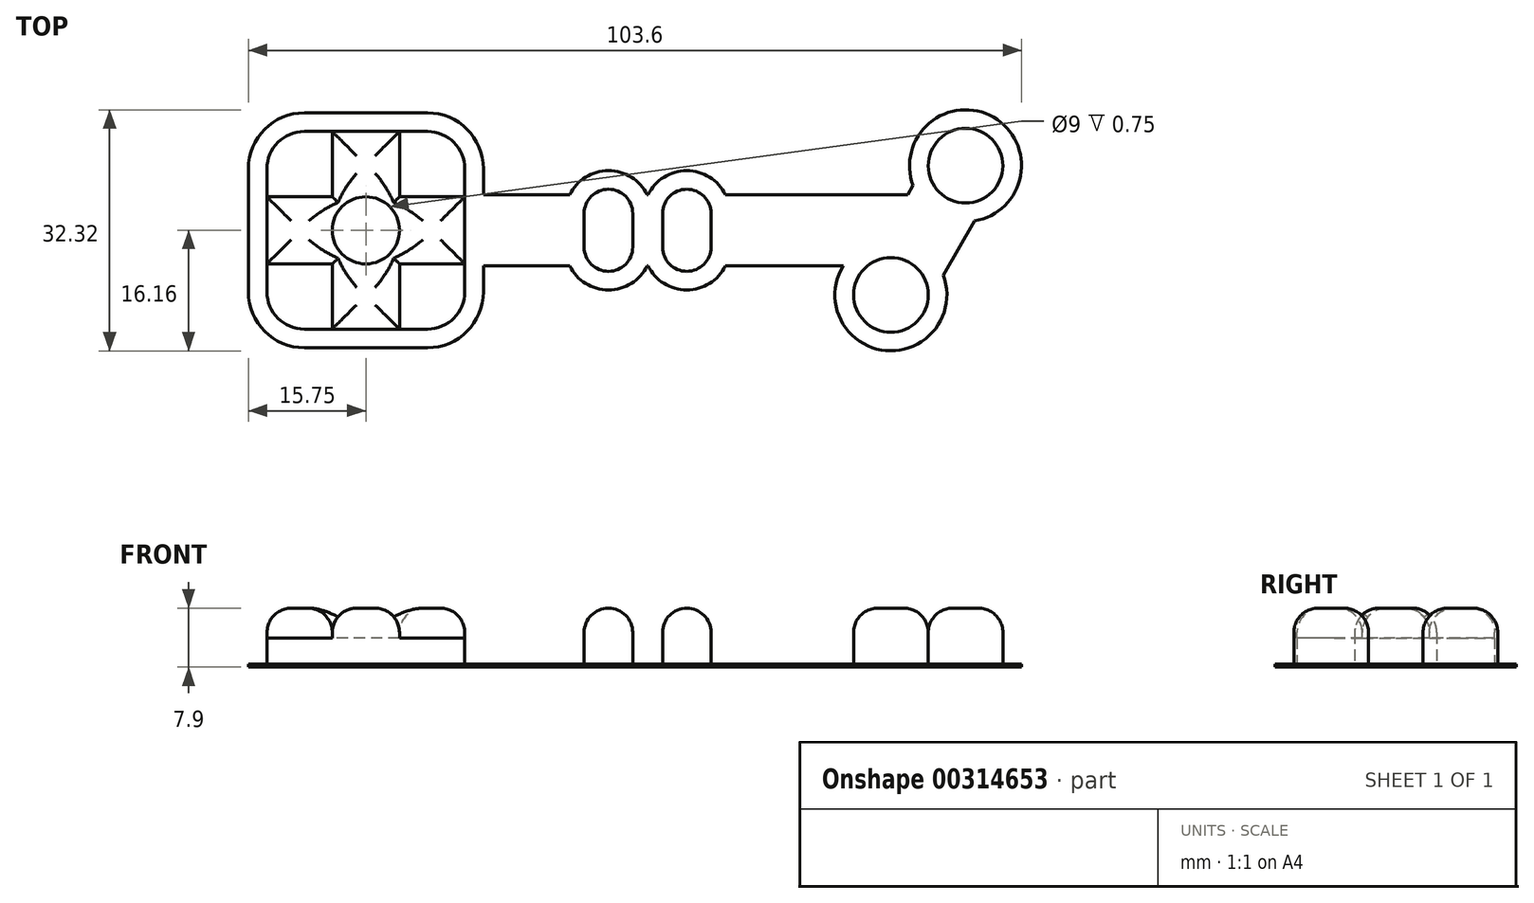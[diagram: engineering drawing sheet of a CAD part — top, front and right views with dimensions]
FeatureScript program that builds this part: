
annotation { "Feature Type Name" : "Feature", "Feature Type Description" : "" }
export const myFeature = defineFeature(function(context is Context, id is Id, definition is map)
    precondition{}
    {
        {
            var Q0;
            Q0=qCreatedBy(makeId("Top.planeOp"),FACE);
            var sketch = newSketch(context, id + "F0", { "sketchPlane" : qUnion([Q0])});
            skLineSegment(sketch, "E0.bottom", {"start": v(8.25, -13.25) * mm, "end": v(-8.25, -13.25) * mm});
            skLineSegment(sketch, "E0.top", {"start": v(8.25, 13.25) * mm, "end": v(-8.25, 13.25) * mm});
            skLineSegment(sketch, "E0.left", {"start": v(13.25, -8.25) * mm, "end": v(13.25, -2.25) * mm});
            skLineSegment(sketch, "E0.right", {"start": v(-13.25, -8.25) * mm, "end": v(-13.25, 8.25) * mm});
            skPoint(sketch, "E0.middle", {"position": v(0, 0) * mm});
            skPoint(sketch, "E1.visualSharp", {"position": v(-13.25, 13.25) * mm});
            skArc(sketch, "E1.filletArc", {"start": v(-8.25, 13.25) * mm, "mid": v(-11.79, 11.79) * mm, "end": v(-13.25, 8.25) * mm});
            skPoint(sketch, "E2.visualSharp", {"position": v(13.25, 13.25) * mm});
            skArc(sketch, "E2.filletArc", {"start": v(13.25, 8.25) * mm, "mid": v(11.79, 11.79) * mm, "end": v(8.25, 13.25) * mm});
            skPoint(sketch, "E3.visualSharp", {"position": v(13.25, -13.25) * mm});
            skArc(sketch, "E3.filletArc", {"start": v(8.25, -13.25) * mm, "mid": v(11.79, -11.79) * mm, "end": v(13.25, -8.25) * mm});
            skPoint(sketch, "E4.visualSharp", {"position": v(-13.25, -13.25) * mm});
            skArc(sketch, "E4.filletArc", {"start": v(-13.25, -8.25) * mm, "mid": v(-11.79, -11.79) * mm, "end": v(-8.25, -13.25) * mm});
            skCircle(sketch, "E5", {"center": v(0, 0) * mm, "radius": 4.5 * mm});
            skLineSegment(sketch, "E6", {"start": v(-4.5, 13.25) * mm, "end": v(-4.5, -13.25) * mm});
            skLineSegment(sketch, "E7", {"start": v(4.5, 13.25) * mm, "end": v(4.5, -13.25) * mm});
            skLineSegment(sketch, "E8", {"start": v(-13.25, 4.5) * mm, "end": v(13.25, 4.5) * mm});
            skLineSegment(sketch, "E9", {"start": v(-13.25, -4.5) * mm, "end": v(13.25, -4.5) * mm});
            skLineSegment(sketch, "E10", {"start": v(-61.71, 0) * mm, "end": v(60.36, 0) * mm, "construction": true});
            skLineSegment(sketch, "E11", {"start": v(13.25, 2.25) * mm, "end": v(29.25, 2.25) * mm});
            skLineSegment(sketch, "E12.bottom", {"start": v(29.25, 2.25) * mm, "end": v(35.75, 2.25) * mm});
            skLineSegment(sketch, "E12.top", {"start": v(29.25, -2.25) * mm, "end": v(35.75, -2.25) * mm});
            skLineSegment(sketch, "E12.left", {"start": v(29.25, 2.25) * mm, "end": v(29.25, -2.25) * mm});
            skLineSegment(sketch, "E12.right", {"start": v(35.75, 2.25) * mm, "end": v(35.75, -2.25) * mm});
            skLineSegment(sketch, "E13", {"start": v(37.75, 8.35) * mm, "end": v(37.75, -9.7) * mm, "construction": true});
            skLineSegment(sketch, "E14.MirrorCS", {"start": v(39.75, 2.25) * mm, "end": v(39.75, -2.25) * mm});
            skLineSegment(sketch, "E15.MirrorCS", {"start": v(46.25, -2.25) * mm, "end": v(39.75, -2.25) * mm});
            skLineSegment(sketch, "E16.MirrorCS", {"start": v(46.25, 2.25) * mm, "end": v(39.75, 2.25) * mm});
            skLineSegment(sketch, "E17.MirrorCS", {"start": v(46.25, 2.25) * mm, "end": v(46.25, -45.9) * mm});
            skLineSegment(sketch, "E18.MirrorCS", {"start": v(13.25, -2.25) * mm, "end": v(29.25, -2.25) * mm});
            skLineSegment(sketch, "E19", {"start": v(35.75, 2.25) * mm, "end": v(39.75, 2.25) * mm});
            skLineSegment(sketch, "E20", {"start": v(39.75, -2.25) * mm, "end": v(35.75, -2.25) * mm});
            skArc(sketch, "E21", {"start": v(35.75, 2.25) * mm, "mid": v(32.5, 5.5) * mm, "end": v(29.25, 2.25) * mm});
            skArc(sketch, "E22.MirrorCS", {"start": v(39.75, 2.25) * mm, "mid": v(43, 5.5) * mm, "end": v(46.25, 2.25) * mm});
            skLineSegment(sketch, "E23.MirrorCS", {"start": v(137.21, 0) * mm, "end": v(15.14, 0) * mm, "construction": true});
            skArc(sketch, "E24.MirrorCS", {"start": v(35.75, -2.25) * mm, "mid": v(32.5, -5.5) * mm, "end": v(29.25, -2.25) * mm});
            skArc(sketch, "E25.MirrorCS", {"start": v(39.75, -2.25) * mm, "mid": v(43, -5.5) * mm, "end": v(46.25, -2.25) * mm});
            skLineSegment(sketch, "E26", {"start": v(46.25, 2.25) * mm, "end": v(74.05, 2.25) * mm});
            skLineSegment(sketch, "E27", {"start": v(80.35, 8.66) * mm, "end": v(70.35, -8.66) * mm, "construction": true});
            skPoint(sketch, "E28", {"position": v(75.35, 0) * mm});
            skLineSegment(sketch, "E29", {"start": v(76.17, 5.92) * mm, "end": v(74.05, 2.25) * mm});
            skLineSegment(sketch, "E30.MirrorCS", {"start": v(80.06, 3.67) * mm, "end": v(74.53, -5.92) * mm});
            skPoint(sketch, "E31", {"position": v(72.75, 0) * mm});
            skPoint(sketch, "E32.orphan", {"position": v(46.25, -2.25) * mm});
            skLineSegment(sketch, "E33", {"start": v(46.25, -2.25) * mm, "end": v(71.45, -2.25) * mm});
            skLineSegment(sketch, "E34", {"start": v(71.45, -2.25) * mm, "end": v(70.63, -3.67) * mm});
            skLineSegment(sketch, "E35", {"start": v(74.05, 2.25) * mm, "end": v(71.45, -2.25) * mm});
            skArc(sketch, "E36", {"start": v(76.17, 5.92) * mm, "mid": v(77.85, 4.33) * mm, "end": v(80.06, 3.67) * mm});
            skArc(sketch, "E37", {"start": v(80.06, 3.67) * mm, "mid": v(82.85, 13) * mm, "end": v(76.17, 5.92) * mm});
            skLineSegment(sketch, "E38", {"start": v(70.63, -3.67) * mm, "end": v(70.63, -3.67) * mm});
            skArc(sketch, "E39", {"start": v(70.63, -3.67) * mm, "mid": v(67.85, -13) * mm, "end": v(74.53, -5.92) * mm});
            skArc(sketch, "E40", {"start": v(74.53, -5.92) * mm, "mid": v(72.85, -4.33) * mm, "end": v(70.63, -3.67) * mm});
            skLineSegment(sketch, "E41", {"start": v(13.25, 2.25) * mm, "end": v(13.25, 8.25) * mm});
            skLineSegment(sketch, "E42", {"start": v(13.25, -2.25) * mm, "end": v(13.25, 2.25) * mm});
            skLineSegment(sketch, "E43.0", {"start": v(37.82, -4.75) * mm, "end": v(37.68, -4.75) * mm});
            skArc(sketch, "E43.1", {"start": v(37.68, -4.75) * mm, "mid": v(32.5, -8) * mm, "end": v(27.32, -4.75) * mm});
            skLineSegment(sketch, "E43.2", {"start": v(15.75, -4.75) * mm, "end": v(27.32, -4.75) * mm});
            skLineSegment(sketch, "E43.3", {"start": v(15.75, -8.25) * mm, "end": v(15.75, -4.75) * mm});
            skArc(sketch, "E43.4", {"start": v(8.25, -15.75) * mm, "mid": v(13.55, -13.55) * mm, "end": v(15.75, -8.25) * mm});
            skLineSegment(sketch, "E43.5", {"start": v(8.25, -15.75) * mm, "end": v(-8.25, -15.75) * mm});
            skLineSegment(sketch, "E43.6", {"start": v(8.25, 15.75) * mm, "end": v(-8.25, 15.75) * mm});
            skArc(sketch, "E43.7", {"start": v(-8.25, 15.75) * mm, "mid": v(-13.55, 13.55) * mm, "end": v(-15.75, 8.25) * mm});
            skLineSegment(sketch, "E43.8", {"start": v(-15.75, -8.25) * mm, "end": v(-15.75, 8.25) * mm});
            skArc(sketch, "E43.9", {"start": v(-15.75, -8.25) * mm, "mid": v(-13.55, -13.55) * mm, "end": v(-8.25, -15.75) * mm});
            skArc(sketch, "E43.10", {"start": v(15.75, 8.25) * mm, "mid": v(13.55, 13.55) * mm, "end": v(8.25, 15.75) * mm});
            skArc(sketch, "E43.11", {"start": v(37.82, -4.75) * mm, "mid": v(43, -8) * mm, "end": v(48.18, -4.75) * mm});
            skLineSegment(sketch, "E43.12", {"start": v(48.18, -4.75) * mm, "end": v(63.95, -4.75) * mm});
            skArc(sketch, "E43.13", {"start": v(63.95, -4.75) * mm, "mid": v(69.65, -16.13) * mm, "end": v(77.36, -6) * mm});
            skLineSegment(sketch, "E43.14", {"start": v(81.56, 1.26) * mm, "end": v(77.36, -6) * mm});
            skArc(sketch, "E43.15", {"start": v(81.56, 1.26) * mm, "mid": v(84.1, 15.16) * mm, "end": v(73.33, 6) * mm});
            skLineSegment(sketch, "E43.16", {"start": v(73.33, 6) * mm, "end": v(72.6, 4.75) * mm});
            skLineSegment(sketch, "E43.17", {"start": v(48.18, 4.75) * mm, "end": v(72.6, 4.75) * mm});
            skArc(sketch, "E43.18", {"start": v(37.82, 4.75) * mm, "mid": v(43, 8) * mm, "end": v(48.18, 4.75) * mm});
            skLineSegment(sketch, "E43.19", {"start": v(37.68, 4.75) * mm, "end": v(37.82, 4.75) * mm});
            skArc(sketch, "E43.20", {"start": v(37.68, 4.75) * mm, "mid": v(32.5, 8) * mm, "end": v(27.32, 4.75) * mm});
            skLineSegment(sketch, "E43.21", {"start": v(15.75, 4.75) * mm, "end": v(27.32, 4.75) * mm});
            skLineSegment(sketch, "E43.22", {"start": v(15.75, 4.75) * mm, "end": v(15.75, 8.25) * mm});
            skSolve(sketch);
        }
        {
            var Q0;
            Q0=makeQuery(id+"F0.imprint","IMPRINT",FACE,{"disambiguationData":[TD([[makeQuery(id+"F0.imprint","IMPRINT",EDGE,{"derivedFrom":sQuery(id+"F0.wireOp",EDGE,"E36")}),1.0]])]});
            var Q1;
            {var subQ0=sQuery(id+"F0.wireOp",EDGE,"E8");var subQ1=sQuery(id+"F0.wireOp",EDGE,"E5");var subQ2=makeQuery(id+"F0.imprint","INTERSECT",VERTEX,{"derivedFrom":[subQ1,subQ0]});Q1=makeQuery(id+"F0.imprint","IMPRINT",FACE,{"disambiguationData":[TD([[makeQuery(id+"F0.imprint","IMPRINT",EDGE,{"disambiguationData":[TD([[subQ2,1.0]])],"derivedFrom":subQ1}),-1.0]])]});}
            var Q2;
            Q2=makeQuery(id+"F0.imprint","IMPRINT",FACE,{"disambiguationData":[TD([[makeQuery(id+"F0.imprint","IMPRINT",EDGE,{"derivedFrom":sQuery(id+"F0.wireOp",EDGE,"E11")}),-1.0]])]});
            var Q3;
            Q3=makeQuery(id+"F0.imprint","IMPRINT",FACE,{"disambiguationData":[TD([[makeQuery(id+"F0.imprint","IMPRINT",EDGE,{"derivedFrom":sQuery(id+"F0.wireOp",EDGE,"E39")}),1.0]])]});
            var Q4;
            {var subQ0=sQuery(id+"F0.wireOp",EDGE,"E4.filletArc");Q4=makeQuery(id+"F0.imprint","IMPRINT",FACE,{"disambiguationData":[TD([[makeQuery(id+"F0.imprint","IMPRINT",EDGE,{"derivedFrom":subQ0}),1.0]])]});}
            var Q5;
            Q5=makeQuery(id+"F0.imprint","IMPRINT",FACE,{"disambiguationData":[TD([[makeQuery(id+"F0.imprint","IMPRINT",EDGE,{"derivedFrom":sQuery(id+"F0.wireOp",EDGE,"E12.top")}),-1.0]])]});
            var Q6;
            {var subQ2=sQuery(id+"F0.wireOp",EDGE,"E26");Q6=makeQuery(id+"F0.imprint","IMPRINT",FACE,{"disambiguationData":[TD([[makeQuery(id+"F0.imprint","IMPRINT",EDGE,{"derivedFrom":subQ2}),-1.0]])]});}
            var Q7;
            {var subQ5=sQuery(id+"F0.wireOp",EDGE,"E2.filletArc");Q7=makeQuery(id+"F0.imprint","IMPRINT",FACE,{"disambiguationData":[TD([[makeQuery(id+"F0.imprint","IMPRINT",EDGE,{"derivedFrom":subQ5}),1.0]])]});}
            var Q8;
            {var subQ0=sQuery(id+"F0.wireOp",EDGE,"E7");var subQ1=sQuery(id+"F0.wireOp",EDGE,"E5");var subQ2=makeQuery(id+"F0.imprint","INTERSECT",VERTEX,{"derivedFrom":[subQ1,subQ0]});Q8=makeQuery(id+"F0.imprint","IMPRINT",FACE,{"disambiguationData":[TD([[makeQuery(id+"F0.imprint","IMPRINT",EDGE,{"disambiguationData":[TD([[subQ2,1.0]])],"derivedFrom":subQ1}),-1.0]])]});}
            var Q9;
            {var subQ0=sQuery(id+"F0.wireOp",EDGE,"E8");var subQ1=sQuery(id+"F0.wireOp",EDGE,"E5");var subQ2=makeQuery(id+"F0.imprint","INTERSECT",VERTEX,{"derivedFrom":[subQ1,subQ0]});Q9=makeQuery(id+"F0.imprint","IMPRINT",FACE,{"disambiguationData":[TD([[makeQuery(id+"F0.imprint","IMPRINT",EDGE,{"disambiguationData":[TD([[subQ2,-1.0]])],"derivedFrom":subQ1}),-1.0]])]});}
            var Q10;
            Q10=makeQuery(id+"F0.imprint","IMPRINT",FACE,{"disambiguationData":[TD([[makeQuery(id+"F0.imprint","IMPRINT",EDGE,{"derivedFrom":sQuery(id+"F0.wireOp",EDGE,"E15.MirrorCS")}),1.0]])]});
            var Q11;
            Q11=makeQuery(id+"F0.imprint","IMPRINT",FACE,{"disambiguationData":[TD([[makeQuery(id+"F0.imprint","IMPRINT",EDGE,{"derivedFrom":sQuery(id+"F0.wireOp",EDGE,"E16.MirrorCS")}),-1.0]])]});
            var Q12;
            {var subQ0=sQuery(id+"F0.wireOp",EDGE,"E6");var subQ1=sQuery(id+"F0.wireOp",EDGE,"E5");var subQ2=makeQuery(id+"F0.imprint","INTERSECT",VERTEX,{"derivedFrom":[subQ1,subQ0]});Q12=makeQuery(id+"F0.imprint","IMPRINT",FACE,{"disambiguationData":[TD([[makeQuery(id+"F0.imprint","IMPRINT",EDGE,{"disambiguationData":[TD([[subQ2,-1.0]])],"derivedFrom":subQ1}),-1.0]])]});}
            var Q13;
            {var subQ17=sQuery(id+"F0.wireOp",EDGE,"E1.filletArc");Q13=makeQuery(id+"F0.imprint","IMPRINT",FACE,{"disambiguationData":[TD([[makeQuery(id+"F0.imprint","IMPRINT",EDGE,{"derivedFrom":subQ17}),-1.0]])]});}
            var Q14;
            {var subQ0=sQuery(id+"F0.wireOp",EDGE,"E3.filletArc");Q14=makeQuery(id+"F0.imprint","IMPRINT",FACE,{"disambiguationData":[TD([[makeQuery(id+"F0.imprint","IMPRINT",EDGE,{"derivedFrom":subQ0}),1.0]])]});}
            var Q15;
            Q15=makeQuery(id+"F0.imprint","IMPRINT",FACE,{"disambiguationData":[TD([[makeQuery(id+"F0.imprint","IMPRINT",EDGE,{"derivedFrom":sQuery(id+"F0.wireOp",EDGE,"E12.right")}),1.0]])]});
            var Q16;
            Q16=makeQuery(id+"F0.imprint","IMPRINT",FACE,{"disambiguationData":[TD([[makeQuery(id+"F0.imprint","IMPRINT",EDGE,{"derivedFrom":sQuery(id+"F0.wireOp",EDGE,"E12.bottom")}),1.0]])]});
            var Q17;
            Q17=makeQuery(id+"F0.imprint","IMPRINT",FACE,{"disambiguationData":[TD([[makeQuery(id+"F0.imprint","IMPRINT",EDGE,{"derivedFrom":sQuery(id+"F0.wireOp",EDGE,"E12.bottom")}),-1.0]])]});
            var Q18;
            {var subQ5=sQuery(id+"F0.wireOp",EDGE,"E1.filletArc");Q18=makeQuery(id+"F0.imprint","IMPRINT",FACE,{"disambiguationData":[TD([[makeQuery(id+"F0.imprint","IMPRINT",EDGE,{"derivedFrom":subQ5}),1.0]])]});}
            var Q19;
            Q19=makeQuery(id+"F0.imprint","IMPRINT",FACE,{"disambiguationData":[TD([[makeQuery(id+"F0.imprint","IMPRINT",EDGE,{"derivedFrom":sQuery(id+"F0.wireOp",EDGE,"E14.MirrorCS")}),1.0]])]});
            var Q20;
            {var subQ2=sQuery(id+"F0.wireOp",EDGE,"E6");var subQ4=sQuery(id+"F0.wireOp",EDGE,"E0.bottom");var subQ5=makeQuery(id+"F0.imprint","INTERSECT",VERTEX,{"derivedFrom":[subQ4,subQ2]});Q20=makeQuery(id+"F0.imprint","IMPRINT",FACE,{"disambiguationData":[TD([[makeQuery(id+"F0.imprint","IMPRINT",EDGE,{"disambiguationData":[TD([[subQ5,1.0]])],"derivedFrom":subQ4}),-1.0]])]});}
            var Q21;
            Q21=makeQuery(id+"F0.imprint","IMPRINT",FACE,{"disambiguationData":[TD([[makeQuery(id+"F0.imprint","IMPRINT",EDGE,{"derivedFrom":sQuery(id+"F0.wireOp",EDGE,"E29")}),1.0]])]});
            var Q22;
            {var subQ5=sQuery(id+"F0.wireOp",EDGE,"E42");Q22=makeQuery(id+"F0.imprint","IMPRINT",FACE,{"disambiguationData":[TD([[makeQuery(id+"F0.imprint","IMPRINT",EDGE,{"derivedFrom":subQ5}),1.0]])]});}
            var Q23;
            {var subQ0=sQuery(id+"F0.wireOp",EDGE,"E5");var subQ1=makeQuery(id+"F0.imprint","INTERSECT",VERTEX,{"derivedFrom":[subQ0,sQuery(id+"F0.wireOp",EDGE,"E8")]});Q23=makeQuery(id+"F0.imprint","IMPRINT",FACE,{"disambiguationData":[TD([[makeQuery(id+"F0.imprint","IMPRINT",EDGE,{"disambiguationData":[TD([[subQ1,1.0]])],"derivedFrom":subQ0}),1.0]])]});}
            var Q24;
            {var subQ2=sQuery(id+"F0.wireOp",EDGE,"E6");var subQ5=sQuery(id+"F0.wireOp",EDGE,"E0.top");var subQ8=makeQuery(id+"F0.imprint","INTERSECT",VERTEX,{"derivedFrom":[subQ5,subQ2]});Q24=makeQuery(id+"F0.imprint","IMPRINT",FACE,{"disambiguationData":[TD([[makeQuery(id+"F0.imprint","IMPRINT",EDGE,{"disambiguationData":[TD([[subQ8,1.0]])],"derivedFrom":subQ5}),1.0]])]});}
            var Q25;
            {var subQ0=sQuery(id+"F0.wireOp",EDGE,"E8");var subQ1=sQuery(id+"F0.wireOp",EDGE,"E0.right");var subQ2=makeQuery(id+"F0.imprint","INTERSECT",VERTEX,{"derivedFrom":[subQ1,subQ0]});Q25=makeQuery(id+"F0.imprint","IMPRINT",FACE,{"disambiguationData":[TD([[makeQuery(id+"F0.imprint","IMPRINT",EDGE,{"disambiguationData":[TD([[subQ2,1.0]])],"derivedFrom":subQ1}),-1.0]])]});}
            extrude(context, id + "F1", {"entities" : qUnion([Q0, Q1, Q2, Q3, Q4, Q5, Q6, Q7, Q8, Q9, Q10, Q11, Q12, Q13, Q14, Q15, Q16, Q17, Q18, Q19, Q20, Q21, Q22, Q23, Q24, Q25]), "depth" : 0.4 * mm});
        }
        {
            var Q0;
            Q0=makeQuery(id+"F1.opExtrude","CAP_FACE",FACE,{"disambiguationData":[OSD([sQuery(id+"F0.wireOp",EDGE,"E43.0"),sQuery(id+"F0.wireOp",EDGE,"E43.1"),sQuery(id+"F0.wireOp",EDGE,"E43.2"),sQuery(id+"F0.wireOp",EDGE,"E43.3"),sQuery(id+"F0.wireOp",EDGE,"E43.4"),sQuery(id+"F0.wireOp",EDGE,"E43.5"),sQuery(id+"F0.wireOp",EDGE,"E43.6"),sQuery(id+"F0.wireOp",EDGE,"E43.7"),sQuery(id+"F0.wireOp",EDGE,"E43.8"),sQuery(id+"F0.wireOp",EDGE,"E43.9"),sQuery(id+"F0.wireOp",EDGE,"E43.10"),sQuery(id+"F0.wireOp",EDGE,"E43.11"),sQuery(id+"F0.wireOp",EDGE,"E43.12"),sQuery(id+"F0.wireOp",EDGE,"E43.13"),sQuery(id+"F0.wireOp",EDGE,"E43.14"),sQuery(id+"F0.wireOp",EDGE,"E43.15"),sQuery(id+"F0.wireOp",EDGE,"E43.16"),sQuery(id+"F0.wireOp",EDGE,"E43.17"),sQuery(id+"F0.wireOp",EDGE,"E43.18"),sQuery(id+"F0.wireOp",EDGE,"E43.19"),sQuery(id+"F0.wireOp",EDGE,"E43.20"),sQuery(id+"F0.wireOp",EDGE,"E43.21"),sQuery(id+"F0.wireOp",EDGE,"E43.22")])],"isStart":false});
            var sketch = newSketch(context, id + "F2", { "sketchPlane" : qUnion([Q0])});
            skLineSegment(sketch, "E44.0", {"start": v(8.25, -13.25) * mm, "end": v(-8.25, -13.25) * mm});
            skLineSegment(sketch, "E44.1", {"start": v(8.25, 13.25) * mm, "end": v(-8.25, 13.25) * mm});
            skLineSegment(sketch, "E44.2", {"start": v(13.25, -8.25) * mm, "end": v(13.25, -2.25) * mm});
            skLineSegment(sketch, "E44.3", {"start": v(-13.25, -8.25) * mm, "end": v(-13.25, 8.25) * mm});
            skPoint(sketch, "E44.4", {"position": v(0, 0) * mm});
            skPoint(sketch, "E44.5", {"position": v(-13.25, 13.25) * mm});
            skArc(sketch, "E44.6", {"start": v(-8.25, 13.25) * mm, "mid": v(-11.79, 11.79) * mm, "end": v(-13.25, 8.25) * mm});
            skPoint(sketch, "E44.7", {"position": v(13.25, 13.25) * mm});
            skArc(sketch, "E44.8", {"start": v(13.25, 8.25) * mm, "mid": v(11.79, 11.79) * mm, "end": v(8.25, 13.25) * mm});
            skPoint(sketch, "E44.9", {"position": v(13.25, -13.25) * mm});
            skArc(sketch, "E44.10", {"start": v(8.25, -13.25) * mm, "mid": v(11.79, -11.79) * mm, "end": v(13.25, -8.25) * mm});
            skPoint(sketch, "E44.11", {"position": v(-13.25, -13.25) * mm});
            skArc(sketch, "E44.12", {"start": v(-13.25, -8.25) * mm, "mid": v(-11.79, -11.79) * mm, "end": v(-8.25, -13.25) * mm});
            skCircle(sketch, "E44.13", {"center": v(0, 0) * mm, "radius": 4.5 * mm});
            skLineSegment(sketch, "E44.14", {"start": v(-4.5, 13.25) * mm, "end": v(-4.5, -13.25) * mm});
            skLineSegment(sketch, "E44.15", {"start": v(4.5, 13.25) * mm, "end": v(4.5, -13.25) * mm});
            skLineSegment(sketch, "E44.16", {"start": v(-13.25, 4.5) * mm, "end": v(13.25, 4.5) * mm});
            skLineSegment(sketch, "E44.17", {"start": v(-13.25, -4.5) * mm, "end": v(13.25, -4.5) * mm});
            skLineSegment(sketch, "E44.19", {"start": v(13.25, 2.25) * mm, "end": v(29.25, 2.25) * mm});
            skLineSegment(sketch, "E44.20", {"start": v(29.25, 2.25) * mm, "end": v(35.75, 2.25) * mm});
            skLineSegment(sketch, "E44.21", {"start": v(29.25, -2.25) * mm, "end": v(35.75, -2.25) * mm});
            skLineSegment(sketch, "E44.22", {"start": v(29.25, 2.25) * mm, "end": v(29.25, -2.25) * mm});
            skLineSegment(sketch, "E44.23", {"start": v(35.75, 2.25) * mm, "end": v(35.75, -2.25) * mm});
            skLineSegment(sketch, "E44.25", {"start": v(39.75, 2.25) * mm, "end": v(39.75, -2.25) * mm});
            skLineSegment(sketch, "E44.26", {"start": v(46.25, -2.25) * mm, "end": v(39.75, -2.25) * mm});
            skLineSegment(sketch, "E44.27", {"start": v(46.25, 2.25) * mm, "end": v(39.75, 2.25) * mm});
            skLineSegment(sketch, "E44.28", {"start": v(46.25, 2.25) * mm, "end": v(46.25, -2.25) * mm});
            skLineSegment(sketch, "E44.29", {"start": v(13.25, -2.25) * mm, "end": v(29.25, -2.25) * mm});
            skLineSegment(sketch, "E44.30", {"start": v(35.75, 2.25) * mm, "end": v(39.75, 2.25) * mm});
            skLineSegment(sketch, "E44.31", {"start": v(39.75, -2.25) * mm, "end": v(35.75, -2.25) * mm});
            skArc(sketch, "E44.32", {"start": v(35.75, 2.25) * mm, "mid": v(32.5, 5.5) * mm, "end": v(29.25, 2.25) * mm});
            skArc(sketch, "E44.33", {"start": v(39.75, 2.25) * mm, "mid": v(43, 5.5) * mm, "end": v(46.25, 2.25) * mm});
            skLineSegment(sketch, "E44.34", {"start": v(80.83, 0) * mm, "end": v(15.14, 0) * mm});
            skArc(sketch, "E44.35", {"start": v(35.75, -2.25) * mm, "mid": v(32.5, -5.5) * mm, "end": v(29.25, -2.25) * mm});
            skArc(sketch, "E44.36", {"start": v(39.75, -2.25) * mm, "mid": v(43, -5.5) * mm, "end": v(46.25, -2.25) * mm});
            skLineSegment(sketch, "E44.37", {"start": v(46.25, 2.25) * mm, "end": v(74.05, 2.25) * mm});
            skLineSegment(sketch, "E44.38", {"start": v(80.35, 8.66) * mm, "end": v(70.35, -8.66) * mm});
            skPoint(sketch, "E44.39", {"position": v(75.35, 0) * mm});
            skLineSegment(sketch, "E44.40", {"start": v(76.17, 5.92) * mm, "end": v(74.05, 2.25) * mm});
            skLineSegment(sketch, "E44.41", {"start": v(80.06, 3.67) * mm, "end": v(74.53, -5.92) * mm});
            skPoint(sketch, "E44.42", {"position": v(72.75, 0) * mm});
            skPoint(sketch, "E44.43", {"position": v(46.25, -2.25) * mm});
            skLineSegment(sketch, "E44.44", {"start": v(46.25, -2.25) * mm, "end": v(71.45, -2.25) * mm});
            skLineSegment(sketch, "E44.45", {"start": v(71.45, -2.25) * mm, "end": v(70.63, -3.67) * mm});
            skLineSegment(sketch, "E44.46", {"start": v(74.05, 2.25) * mm, "end": v(71.45, -2.25) * mm});
            skArc(sketch, "E44.47", {"start": v(76.17, 5.92) * mm, "mid": v(77.85, 4.33) * mm, "end": v(80.06, 3.67) * mm});
            skArc(sketch, "E44.48", {"start": v(80.06, 3.67) * mm, "mid": v(82.85, 13) * mm, "end": v(76.17, 5.92) * mm});
            skPoint(sketch, "E44.49", {"position": v(70.63, -3.67) * mm});
            skArc(sketch, "E44.50", {"start": v(70.63, -3.67) * mm, "mid": v(67.85, -13) * mm, "end": v(74.53, -5.92) * mm});
            skArc(sketch, "E44.51", {"start": v(74.53, -5.92) * mm, "mid": v(72.85, -4.33) * mm, "end": v(70.63, -3.67) * mm});
            skLineSegment(sketch, "E44.52", {"start": v(13.25, 2.25) * mm, "end": v(13.25, 8.25) * mm});
            skLineSegment(sketch, "E44.53", {"start": v(13.25, -2.25) * mm, "end": v(13.25, 2.25) * mm});
            skLineSegment(sketch, "E44.54", {"start": v(37.82, -4.75) * mm, "end": v(37.68, -4.75) * mm});
            skArc(sketch, "E44.55", {"start": v(37.68, -4.75) * mm, "mid": v(32.5, -8) * mm, "end": v(27.32, -4.75) * mm});
            skLineSegment(sketch, "E44.56", {"start": v(15.75, -4.75) * mm, "end": v(27.32, -4.75) * mm});
            skLineSegment(sketch, "E44.57", {"start": v(15.75, -8.25) * mm, "end": v(15.75, -4.75) * mm});
            skArc(sketch, "E44.58", {"start": v(8.25, -15.75) * mm, "mid": v(13.55, -13.55) * mm, "end": v(15.75, -8.25) * mm});
            skLineSegment(sketch, "E44.59", {"start": v(8.25, -15.75) * mm, "end": v(-8.25, -15.75) * mm});
            skLineSegment(sketch, "E44.60", {"start": v(8.25, 15.75) * mm, "end": v(-8.25, 15.75) * mm});
            skArc(sketch, "E44.61", {"start": v(-8.25, 15.75) * mm, "mid": v(-13.55, 13.55) * mm, "end": v(-15.75, 8.25) * mm});
            skLineSegment(sketch, "E44.62", {"start": v(-15.75, -8.25) * mm, "end": v(-15.75, 8.25) * mm});
            skArc(sketch, "E44.63", {"start": v(-15.75, -8.25) * mm, "mid": v(-13.55, -13.55) * mm, "end": v(-8.25, -15.75) * mm});
            skArc(sketch, "E44.64", {"start": v(15.75, 8.25) * mm, "mid": v(13.55, 13.55) * mm, "end": v(8.25, 15.75) * mm});
            skArc(sketch, "E44.65", {"start": v(37.82, -4.75) * mm, "mid": v(43, -8) * mm, "end": v(48.18, -4.75) * mm});
            skLineSegment(sketch, "E44.66", {"start": v(48.18, -4.75) * mm, "end": v(63.95, -4.75) * mm});
            skArc(sketch, "E44.67", {"start": v(63.95, -4.75) * mm, "mid": v(69.65, -16.13) * mm, "end": v(77.36, -6) * mm});
            skLineSegment(sketch, "E44.68", {"start": v(81.56, 1.26) * mm, "end": v(77.36, -6) * mm});
            skArc(sketch, "E44.69", {"start": v(81.56, 1.26) * mm, "mid": v(84.1, 15.16) * mm, "end": v(73.33, 6) * mm});
            skLineSegment(sketch, "E44.70", {"start": v(73.33, 6) * mm, "end": v(72.6, 4.75) * mm});
            skLineSegment(sketch, "E44.71", {"start": v(48.18, 4.75) * mm, "end": v(72.6, 4.75) * mm});
            skArc(sketch, "E44.72", {"start": v(37.82, 4.75) * mm, "mid": v(43, 8) * mm, "end": v(48.18, 4.75) * mm});
            skLineSegment(sketch, "E44.73", {"start": v(37.68, 4.75) * mm, "end": v(37.82, 4.75) * mm});
            skArc(sketch, "E44.74", {"start": v(37.68, 4.75) * mm, "mid": v(32.5, 8) * mm, "end": v(27.32, 4.75) * mm});
            skLineSegment(sketch, "E44.75", {"start": v(15.75, 4.75) * mm, "end": v(27.32, 4.75) * mm});
            skLineSegment(sketch, "E44.76", {"start": v(15.75, 4.75) * mm, "end": v(15.75, 8.25) * mm});
            skSolve(sketch);
        }
        {
            var Q0;
            {var subQ5=sQuery(id+"F2.wireOp",EDGE,"E44.6");Q0=makeQuery(id+"F2.imprint","IMPRINT",FACE,{"disambiguationData":[TD([[makeQuery(id+"F2.imprint","IMPRINT",EDGE,{"derivedFrom":subQ5}),1.0]])]});}
            var Q1;
            {var subQ2=sQuery(id+"F2.wireOp",EDGE,"E44.14");var subQ5=sQuery(id+"F2.wireOp",EDGE,"E44.1");var subQ8=makeQuery(id+"F2.imprint","INTERSECT",VERTEX,{"derivedFrom":[subQ5,subQ2]});Q1=makeQuery(id+"F2.imprint","IMPRINT",FACE,{"disambiguationData":[TD([[makeQuery(id+"F2.imprint","IMPRINT",EDGE,{"disambiguationData":[TD([[subQ8,1.0]])],"derivedFrom":subQ5}),1.0]])]});}
            var Q2;
            {var subQ5=sQuery(id+"F2.wireOp",EDGE,"E44.8");Q2=makeQuery(id+"F2.imprint","IMPRINT",FACE,{"disambiguationData":[TD([[makeQuery(id+"F2.imprint","IMPRINT",EDGE,{"derivedFrom":subQ5}),1.0]])]});}
            var Q3;
            {var subQ8=sQuery(id+"F2.wireOp",EDGE,"E44.53");Q3=makeQuery(id+"F2.imprint","IMPRINT",FACE,{"disambiguationData":[TD([[makeQuery(id+"F2.imprint","IMPRINT",EDGE,{"derivedFrom":subQ8}),1.0]])]});}
            var Q4;
            {var subQ0=sQuery(id+"F2.wireOp",EDGE,"E44.10");Q4=makeQuery(id+"F2.imprint","IMPRINT",FACE,{"disambiguationData":[TD([[makeQuery(id+"F2.imprint","IMPRINT",EDGE,{"derivedFrom":subQ0}),1.0]])]});}
            var Q5;
            {var subQ2=sQuery(id+"F2.wireOp",EDGE,"E44.14");var subQ4=sQuery(id+"F2.wireOp",EDGE,"E44.0");var subQ5=makeQuery(id+"F2.imprint","INTERSECT",VERTEX,{"derivedFrom":[subQ4,subQ2]});Q5=makeQuery(id+"F2.imprint","IMPRINT",FACE,{"disambiguationData":[TD([[makeQuery(id+"F2.imprint","IMPRINT",EDGE,{"disambiguationData":[TD([[subQ5,1.0]])],"derivedFrom":subQ4}),-1.0]])]});}
            var Q6;
            {var subQ0=sQuery(id+"F2.wireOp",EDGE,"E44.12");Q6=makeQuery(id+"F2.imprint","IMPRINT",FACE,{"disambiguationData":[TD([[makeQuery(id+"F2.imprint","IMPRINT",EDGE,{"derivedFrom":subQ0}),1.0]])]});}
            var Q7;
            {var subQ0=sQuery(id+"F2.wireOp",EDGE,"E44.14");var subQ1=sQuery(id+"F2.wireOp",EDGE,"E44.13");var subQ2=makeQuery(id+"F2.imprint","INTERSECT",VERTEX,{"derivedFrom":[subQ1,subQ0]});Q7=makeQuery(id+"F2.imprint","IMPRINT",FACE,{"disambiguationData":[TD([[makeQuery(id+"F2.imprint","IMPRINT",EDGE,{"disambiguationData":[TD([[subQ2,-1.0]])],"derivedFrom":subQ1}),-1.0]])]});}
            var Q8;
            {var subQ0=sQuery(id+"F2.wireOp",EDGE,"E44.15");var subQ1=sQuery(id+"F2.wireOp",EDGE,"E44.13");var subQ2=makeQuery(id+"F2.imprint","INTERSECT",VERTEX,{"derivedFrom":[subQ1,subQ0]});Q8=makeQuery(id+"F2.imprint","IMPRINT",FACE,{"disambiguationData":[TD([[makeQuery(id+"F2.imprint","IMPRINT",EDGE,{"disambiguationData":[TD([[subQ2,1.0]])],"derivedFrom":subQ1}),-1.0]])]});}
            var Q9;
            {var subQ0=sQuery(id+"F2.wireOp",EDGE,"E44.16");var subQ1=sQuery(id+"F2.wireOp",EDGE,"E44.13");var subQ2=makeQuery(id+"F2.imprint","INTERSECT",VERTEX,{"derivedFrom":[subQ1,subQ0]});Q9=makeQuery(id+"F2.imprint","IMPRINT",FACE,{"disambiguationData":[TD([[makeQuery(id+"F2.imprint","IMPRINT",EDGE,{"disambiguationData":[TD([[subQ2,-1.0]])],"derivedFrom":subQ1}),-1.0]])]});}
            var Q10;
            {var subQ0=sQuery(id+"F2.wireOp",EDGE,"E44.16");var subQ1=sQuery(id+"F2.wireOp",EDGE,"E44.3");var subQ2=makeQuery(id+"F2.imprint","INTERSECT",VERTEX,{"derivedFrom":[subQ1,subQ0]});Q10=makeQuery(id+"F2.imprint","IMPRINT",FACE,{"disambiguationData":[TD([[makeQuery(id+"F2.imprint","IMPRINT",EDGE,{"disambiguationData":[TD([[subQ2,1.0]])],"derivedFrom":subQ1}),-1.0]])]});}
            var Q11;
            {var subQ0=sQuery(id+"F2.wireOp",EDGE,"E44.16");var subQ1=sQuery(id+"F2.wireOp",EDGE,"E44.13");var subQ2=makeQuery(id+"F2.imprint","INTERSECT",VERTEX,{"derivedFrom":[subQ1,subQ0]});Q11=makeQuery(id+"F2.imprint","IMPRINT",FACE,{"disambiguationData":[TD([[makeQuery(id+"F2.imprint","IMPRINT",EDGE,{"disambiguationData":[TD([[subQ2,1.0]])],"derivedFrom":subQ1}),-1.0]])]});}
            var Q12;
            {var subQ0=sQuery(id+"F2.wireOp",EDGE,"E44.13");var subQ1=makeQuery(id+"F2.imprint","INTERSECT",VERTEX,{"derivedFrom":[subQ0,sQuery(id+"F2.wireOp",EDGE,"E44.16")]});Q12=makeQuery(id+"F2.imprint","IMPRINT",FACE,{"disambiguationData":[TD([[makeQuery(id+"F2.imprint","IMPRINT",EDGE,{"disambiguationData":[TD([[subQ1,1.0]])],"derivedFrom":subQ0}),1.0]])]});}
            var Q13;
            {var subQ0=sQuery(id+"F2.wireOp",EDGE,"E44.21");Q13=makeQuery(id+"F2.imprint","IMPRINT",FACE,{"disambiguationData":[TD([[makeQuery(id+"F2.imprint","IMPRINT",EDGE,{"derivedFrom":subQ0}),1.0]])]});}
            var Q14;
            {var subQ0=sQuery(id+"F2.wireOp",EDGE,"E44.20");Q14=makeQuery(id+"F2.imprint","IMPRINT",FACE,{"disambiguationData":[TD([[makeQuery(id+"F2.imprint","IMPRINT",EDGE,{"derivedFrom":subQ0}),-1.0]])]});}
            var Q15;
            Q15=makeQuery(id+"F2.imprint","IMPRINT",FACE,{"disambiguationData":[TD([[makeQuery(id+"F2.imprint","IMPRINT",EDGE,{"derivedFrom":sQuery(id+"F2.wireOp",EDGE,"E44.20")}),1.0]])]});
            var Q16;
            Q16=makeQuery(id+"F2.imprint","IMPRINT",FACE,{"disambiguationData":[TD([[makeQuery(id+"F2.imprint","IMPRINT",EDGE,{"derivedFrom":sQuery(id+"F2.wireOp",EDGE,"E44.21")}),-1.0]])]});
            var Q17;
            Q17=makeQuery(id+"F2.imprint","IMPRINT",FACE,{"disambiguationData":[TD([[makeQuery(id+"F2.imprint","IMPRINT",EDGE,{"derivedFrom":sQuery(id+"F2.wireOp",EDGE,"E44.26")}),1.0]])]});
            var Q18;
            {var subQ1=sQuery(id+"F2.wireOp",EDGE,"E44.26");Q18=makeQuery(id+"F2.imprint","IMPRINT",FACE,{"disambiguationData":[TD([[makeQuery(id+"F2.imprint","IMPRINT",EDGE,{"derivedFrom":subQ1}),-1.0]])]});}
            var Q19;
            {var subQ1=sQuery(id+"F2.wireOp",EDGE,"E44.27");Q19=makeQuery(id+"F2.imprint","IMPRINT",FACE,{"disambiguationData":[TD([[makeQuery(id+"F2.imprint","IMPRINT",EDGE,{"derivedFrom":subQ1}),1.0]])]});}
            var Q20;
            Q20=makeQuery(id+"F2.imprint","IMPRINT",FACE,{"disambiguationData":[TD([[makeQuery(id+"F2.imprint","IMPRINT",EDGE,{"derivedFrom":sQuery(id+"F2.wireOp",EDGE,"E44.27")}),-1.0]])]});
            var Q21;
            {var subQ0=sQuery(id+"F2.wireOp",EDGE,"E44.50");Q21=makeQuery(id+"F2.imprint","IMPRINT",FACE,{"disambiguationData":[TD([[makeQuery(id+"F2.imprint","IMPRINT",EDGE,{"derivedFrom":subQ0}),1.0]])]});}
            var Q22;
            {var subQ0=sQuery(id+"F2.wireOp",EDGE,"E44.48");Q22=makeQuery(id+"F2.imprint","IMPRINT",FACE,{"disambiguationData":[TD([[makeQuery(id+"F2.imprint","IMPRINT",EDGE,{"derivedFrom":subQ0}),1.0]])]});}
            extrude(context, id + "F3", {"entities" : qUnion([Q0, Q1, Q2, Q3, Q4, Q5, Q6, Q7, Q8, Q9, Q10, Q11, Q12, Q13, Q14, Q15, Q16, Q17, Q18, Q19, Q20, Q21, Q22]), "operationType" : NewBodyOperationType.ADD, "depth" : 7.5 * mm});
        }
        {
            var Q0;
            Q0=makeQuery(id+"F3.opExtrude","CAP_FACE",FACE,{"disambiguationData":[OSD([sQuery(id+"F2.wireOp",EDGE,"E44.0"),sQuery(id+"F2.wireOp",EDGE,"E44.1"),sQuery(id+"F2.wireOp",EDGE,"E44.2"),sQuery(id+"F2.wireOp",EDGE,"E44.3"),sQuery(id+"F2.wireOp",EDGE,"E44.6"),sQuery(id+"F2.wireOp",EDGE,"E44.8"),sQuery(id+"F2.wireOp",EDGE,"E44.10"),sQuery(id+"F2.wireOp",EDGE,"E44.12"),sQuery(id+"F2.wireOp",EDGE,"E44.52"),sQuery(id+"F2.wireOp",EDGE,"E44.53")])],"isStart":false});
            var sketch = newSketch(context, id + "F4", { "sketchPlane" : qUnion([Q0])});
            skLineSegment(sketch, "E45.0", {"start": v(8.25, -13.25) * mm, "end": v(-8.25, -13.25) * mm});
            skLineSegment(sketch, "E45.1", {"start": v(8.25, 13.25) * mm, "end": v(-8.25, 13.25) * mm});
            skLineSegment(sketch, "E45.2", {"start": v(13.25, -8.25) * mm, "end": v(13.25, -2.25) * mm});
            skLineSegment(sketch, "E45.3", {"start": v(-13.25, -8.25) * mm, "end": v(-13.25, 8.25) * mm});
            skPoint(sketch, "E45.4", {"position": v(0, 0) * mm});
            skPoint(sketch, "E45.5", {"position": v(-13.25, 13.25) * mm});
            skArc(sketch, "E45.6", {"start": v(-8.25, 13.25) * mm, "mid": v(-11.79, 11.79) * mm, "end": v(-13.25, 8.25) * mm});
            skPoint(sketch, "E45.7", {"position": v(13.25, 13.25) * mm});
            skArc(sketch, "E45.8", {"start": v(13.25, 8.25) * mm, "mid": v(11.79, 11.79) * mm, "end": v(8.25, 13.25) * mm});
            skPoint(sketch, "E45.9", {"position": v(13.25, -13.25) * mm});
            skArc(sketch, "E45.10", {"start": v(8.25, -13.25) * mm, "mid": v(11.79, -11.79) * mm, "end": v(13.25, -8.25) * mm});
            skPoint(sketch, "E45.11", {"position": v(-13.25, -13.25) * mm});
            skArc(sketch, "E45.12", {"start": v(-13.25, -8.25) * mm, "mid": v(-11.79, -11.79) * mm, "end": v(-8.25, -13.25) * mm});
            skCircle(sketch, "E45.13", {"center": v(0, 0) * mm, "radius": 4.5 * mm});
            skLineSegment(sketch, "E45.14", {"start": v(-4.5, 13.25) * mm, "end": v(-4.5, -13.25) * mm});
            skLineSegment(sketch, "E45.15", {"start": v(4.5, 13.25) * mm, "end": v(4.5, -13.25) * mm});
            skLineSegment(sketch, "E45.16", {"start": v(-13.25, 4.5) * mm, "end": v(13.25, 4.5) * mm});
            skLineSegment(sketch, "E45.17", {"start": v(-13.25, -4.5) * mm, "end": v(13.25, -4.5) * mm});
            skLineSegment(sketch, "E45.52", {"start": v(13.25, 2.25) * mm, "end": v(13.25, 8.25) * mm});
            skLineSegment(sketch, "E45.53", {"start": v(13.25, -2.25) * mm, "end": v(13.25, 2.25) * mm});
            skLineSegment(sketch, "E45.57", {"start": v(15.75, -8.25) * mm, "end": v(15.75, -4.75) * mm});
            skArc(sketch, "E45.58", {"start": v(8.25, -15.75) * mm, "mid": v(13.55, -13.55) * mm, "end": v(15.75, -8.25) * mm});
            skLineSegment(sketch, "E45.59", {"start": v(8.25, -15.75) * mm, "end": v(-8.25, -15.75) * mm});
            skLineSegment(sketch, "E45.60", {"start": v(8.25, 15.75) * mm, "end": v(-8.25, 15.75) * mm});
            skArc(sketch, "E45.61", {"start": v(-8.25, 15.75) * mm, "mid": v(-13.55, 13.55) * mm, "end": v(-15.75, 8.25) * mm});
            skLineSegment(sketch, "E45.62", {"start": v(-15.75, -8.25) * mm, "end": v(-15.75, 8.25) * mm});
            skArc(sketch, "E45.63", {"start": v(-15.75, -8.25) * mm, "mid": v(-13.55, -13.55) * mm, "end": v(-8.25, -15.75) * mm});
            skArc(sketch, "E45.64", {"start": v(15.75, 8.25) * mm, "mid": v(13.55, 13.55) * mm, "end": v(8.25, 15.75) * mm});
            skLineSegment(sketch, "E45.76", {"start": v(15.75, 4.75) * mm, "end": v(15.75, 8.25) * mm});
            skSolve(sketch);
        }
        {
            var Q0;
            {var subQ5=sQuery(id+"F4.wireOp",EDGE,"E45.8");Q0=makeQuery(id+"F4.imprint","IMPRINT",FACE,{"disambiguationData":[TD([[makeQuery(id+"F4.imprint","IMPRINT",EDGE,{"derivedFrom":subQ5}),1.0]])]});}
            var Q1;
            {var subQ5=sQuery(id+"F4.wireOp",EDGE,"E45.6");Q1=makeQuery(id+"F4.imprint","IMPRINT",FACE,{"disambiguationData":[TD([[makeQuery(id+"F4.imprint","IMPRINT",EDGE,{"derivedFrom":subQ5}),1.0]])]});}
            var Q2;
            {var subQ0=sQuery(id+"F4.wireOp",EDGE,"E45.12");Q2=makeQuery(id+"F4.imprint","IMPRINT",FACE,{"disambiguationData":[TD([[makeQuery(id+"F4.imprint","IMPRINT",EDGE,{"derivedFrom":subQ0}),1.0]])]});}
            var Q3;
            {var subQ0=sQuery(id+"F4.wireOp",EDGE,"E45.10");Q3=makeQuery(id+"F4.imprint","IMPRINT",FACE,{"disambiguationData":[TD([[makeQuery(id+"F4.imprint","IMPRINT",EDGE,{"derivedFrom":subQ0}),1.0]])]});}
            var Q4;
            {var subQ0=sQuery(id+"F4.wireOp",EDGE,"E45.13");var subQ1=makeQuery(id+"F4.imprint","INTERSECT",VERTEX,{"derivedFrom":[subQ0,sQuery(id+"F4.wireOp",EDGE,"E45.16")]});Q4=makeQuery(id+"F4.imprint","IMPRINT",FACE,{"disambiguationData":[TD([[makeQuery(id+"F4.imprint","IMPRINT",EDGE,{"disambiguationData":[TD([[subQ1,1.0]])],"derivedFrom":subQ0}),1.0]])]});}
            extrude(context, id + "F5", {"entities" : qUnion([Q0, Q1, Q2, Q3, Q4]), "operationType" : NewBodyOperationType.REMOVE, "oppositeDirection" : true, "depth" : 4 * mm});
        }
        {
            var Q0;
            Q0=makeQuery(id+"F3.opExtrude","CAP_FACE",FACE,{"disambiguationData":[OSD([sQuery(id+"F2.wireOp",EDGE,"E44.0"),sQuery(id+"F2.wireOp",EDGE,"E44.1"),sQuery(id+"F2.wireOp",EDGE,"E44.2"),sQuery(id+"F2.wireOp",EDGE,"E44.3"),sQuery(id+"F2.wireOp",EDGE,"E44.6"),sQuery(id+"F2.wireOp",EDGE,"E44.8"),sQuery(id+"F2.wireOp",EDGE,"E44.10"),sQuery(id+"F2.wireOp",EDGE,"E44.12"),sQuery(id+"F2.wireOp",EDGE,"E44.52"),sQuery(id+"F2.wireOp",EDGE,"E44.53")])],"isStart":false});
            var Q1;
            Q1=makeQuery(id+"F3.opExtrude","CAP_EDGE",EDGE,{"disambiguationData":[OSD([sQuery(id+"F2.wireOp",EDGE,"E44.23")])],"isStart":false});
            var Q2;
            Q2=makeQuery(id+"F3.opExtrude","CAP_FACE",FACE,{"disambiguationData":[OSD([sQuery(id+"F2.wireOp",EDGE,"E44.25"),sQuery(id+"F2.wireOp",EDGE,"E44.28"),sQuery(id+"F2.wireOp",EDGE,"E44.33"),sQuery(id+"F2.wireOp",EDGE,"E44.36")])],"isStart":false});
            var Q3;
            Q3=makeQuery(id+"F3.opExtrude","CAP_FACE",FACE,{"disambiguationData":[OSD([sQuery(id+"F2.wireOp",EDGE,"E44.50"),sQuery(id+"F2.wireOp",EDGE,"E44.51")])],"isStart":false});
            var Q4;
            Q4=makeQuery(id+"F3.opExtrude","CAP_FACE",FACE,{"disambiguationData":[OSD([sQuery(id+"F2.wireOp",EDGE,"E44.47"),sQuery(id+"F2.wireOp",EDGE,"E44.48")])],"isStart":false});
            fillet(context, id + "F6", {"entities" : qUnion([Q0, Q1, Q2, Q3, Q4]), "radius" : 3.25 * mm, "tangentPropagation" : true, "allowEdgeOverflow" : false});
        }
        {
            var Q0;
            Q0=qCreatedBy(makeId("Top.planeOp"),FACE);
            var sketch = newSketch(context, id + "F7", { "sketchPlane" : qUnion([Q0])});
            skFitSpline(sketch, "E46", {"points": [v(-45.08, 35.97) * mm, v(-60.3, 35.88) * mm, v(-65.66, 35.78) * mm, v(-64.59, 38.6) * mm, v(-60.1, 39.58) * mm, v(-63.71, 40.66) * mm, v(-60.1, 42.31) * mm, v(-62.93, 42.5) * mm, v(-52.89, 51.97) * mm, v(-54.93, 47.87) * mm, v(-46.25, 43.39) * mm, v(-44.6, 39.97) * mm, v(-46.64, 39.39) * mm, v(-43.33, 39.1) * mm, v(-45.28, 38.02) * mm, v(-42.35, 37.24) * mm, v(-45.08, 35.97) * mm]});
            skLineSegment(sketch, "E47", {"start": v(-18.94, 64.96) * mm, "end": v(-18.94, 27.86) * mm});
            skSolve(sketch);
        }
        {
            var Q0;
            Q0=sQuery(id+"F7.wireOp",EDGE,"E46");
            var Q1;
            Q1=sQuery(id+"F7.wireOp",EDGE,"E47");
            revolve(context, id + "F8", {"bodyType" : ToolBodyType.SURFACE, "surfaceEntities" : qUnion([Q0]), "axis" : qUnion([Q1]), "revolveType" : RevolveType.ONE_DIRECTION, "angle" : 180 * degree});
        }
    });
